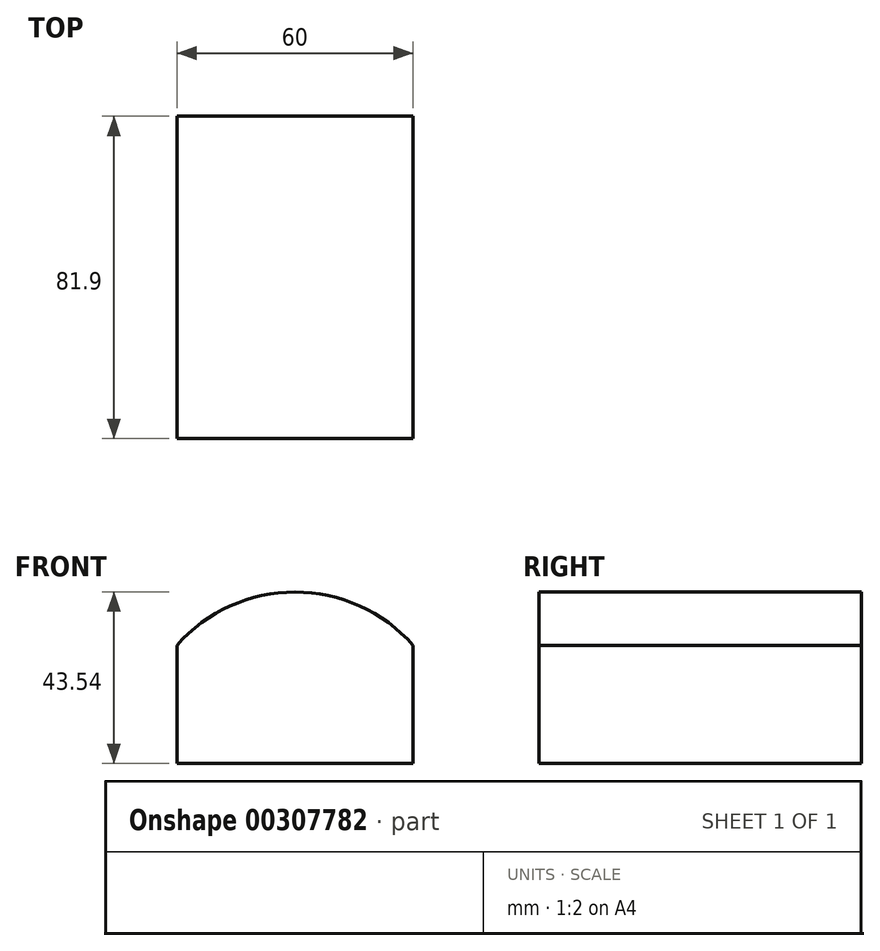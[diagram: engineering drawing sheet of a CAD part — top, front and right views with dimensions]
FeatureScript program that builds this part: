
annotation { "Feature Type Name" : "Feature", "Feature Type Description" : "" }
export const myFeature = defineFeature(function(context is Context, id is Id, definition is map)
    precondition{}
    {
        {
            var Q0;
            Q0=qCreatedBy(makeId("Front.planeOp"),FACE);
            var sketch = newSketch(context, id + "F0", { "sketchPlane" : qUnion([Q0])});
            skLineSegment(sketch, "E0.bottom", {"start": v(-30.8, 13.18) * mm, "end": v(29.2, 13.18) * mm});
            skLineSegment(sketch, "E0.top", {"start": v(-30.8, -16.82) * mm, "end": v(29.2, -16.82) * mm});
            skLineSegment(sketch, "E0.left", {"start": v(-30.8, 13.18) * mm, "end": v(-30.8, -16.82) * mm});
            skLineSegment(sketch, "E0.right", {"start": v(29.2, 13.18) * mm, "end": v(29.2, -16.82) * mm});
            skLineSegment(sketch, "E1.left", {"start": v(29.2, 0) * mm, "end": v(29.2, 2.17) * mm});
            skLineSegment(sketch, "E1.right", {"start": v(29.2, 0) * mm, "end": v(29.2, 2.17) * mm});
            skArc(sketch, "E2", {"start": v(29.2, 13.18) * mm, "mid": v(-0.8, 26.72) * mm, "end": v(-30.8, 13.18) * mm});
            skSolve(sketch);
        }
        {
            var Q0;
            {var subQ1=sQuery(id+"F0.wireOp",EDGE,"E0.bottom");Q0=makeQuery(id+"F0.imprint","IMPRINT",FACE,{"disambiguationData":[TD([[makeQuery(id+"F0.imprint","IMPRINT",EDGE,{"derivedFrom":subQ1}),-1.0]])]});}
            var Q1;
            Q1=makeQuery(id+"F0.imprint","IMPRINT",FACE,{"disambiguationData":[TD([[makeQuery(id+"F0.imprint","IMPRINT",EDGE,{"derivedFrom":sQuery(id+"F0.wireOp",EDGE,"E0.bottom")}),1.0]])]});
            extrude(context, id + "F1", {"entities" : qUnion([Q0, Q1]), "depth" : 81.9 * mm});
        }
    });
